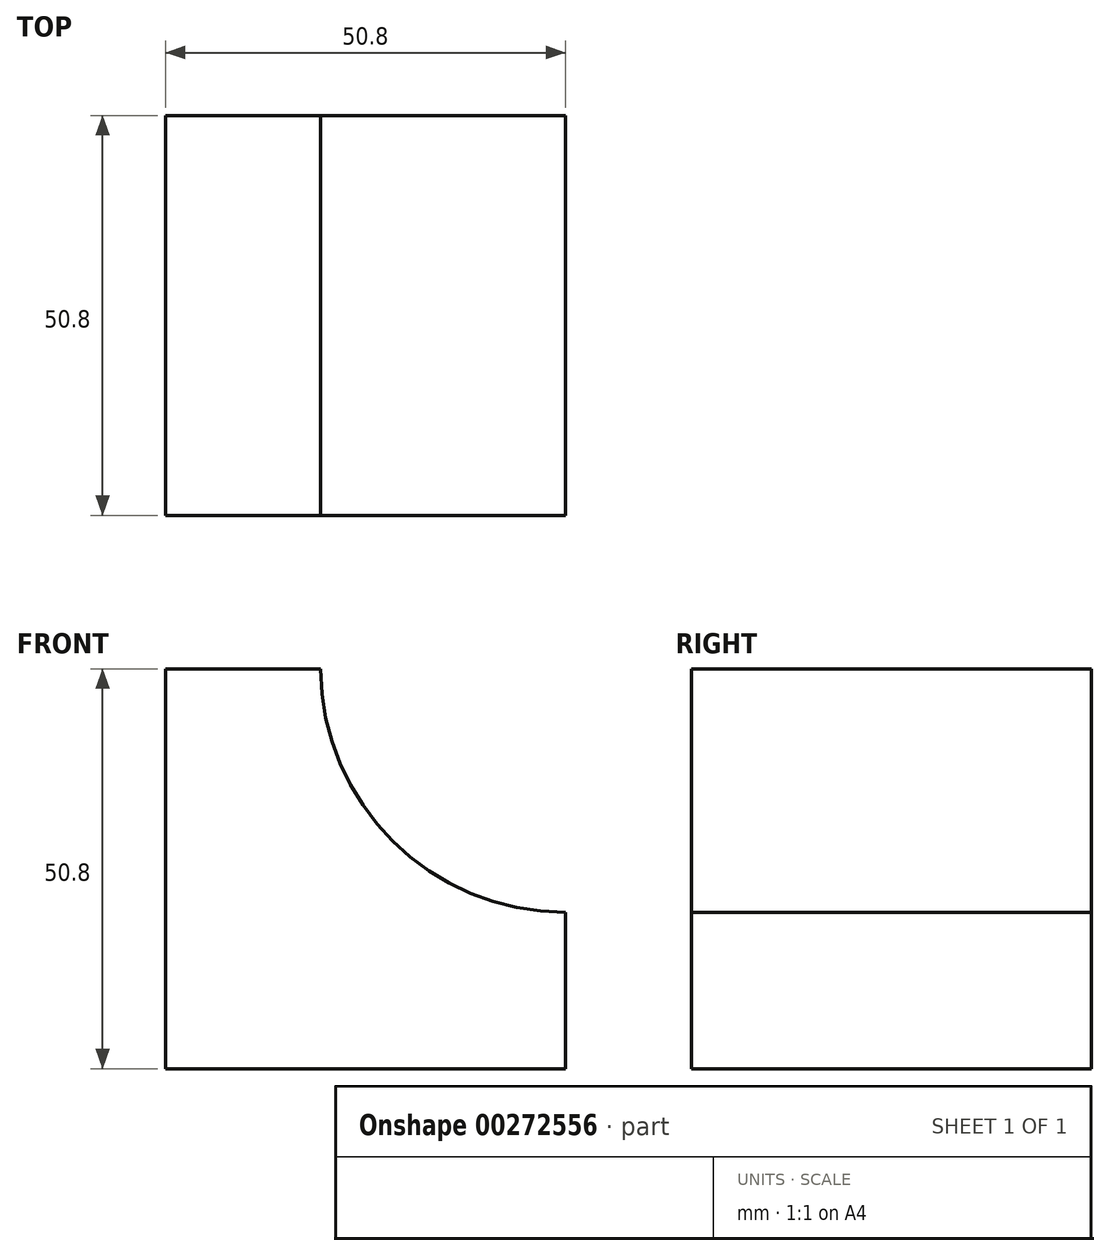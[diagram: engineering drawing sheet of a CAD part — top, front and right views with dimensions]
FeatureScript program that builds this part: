
annotation { "Feature Type Name" : "Feature", "Feature Type Description" : "" }
export const myFeature = defineFeature(function(context is Context, id is Id, definition is map)
    precondition{}
    {
        {
            var Q0;
            Q0=qCreatedBy(makeId("Front.planeOp"),FACE);
            var sketch = newSketch(context, id + "F0", { "sketchPlane" : qUnion([Q0])});
            skLineSegment(sketch, "E0", {"start": v(0, 0) * mm, "end": v(-50.8, 0) * mm});
            skLineSegment(sketch, "E1", {"start": v(-50.8, 0) * mm, "end": v(-50.8, 50.8) * mm});
            skLineSegment(sketch, "E2", {"start": v(-50.8, 50.8) * mm, "end": v(-31.13, 50.8) * mm});
            skLineSegment(sketch, "E3", {"start": v(0, 19.86) * mm, "end": v(0, 0) * mm});
            skArc(sketch, "E4", {"start": v(-31.13, 50.8) * mm, "mid": v(-21.94, 28.91) * mm, "end": v(0, 19.86) * mm});
            skSolve(sketch);
        }
        {
            var Q0;
            Q0=makeQuery(id+"F0.imprint","IMPRINT",FACE,{"disambiguationData":[TD([[makeQuery(id+"F0.imprint","IMPRINT",EDGE,{"derivedFrom":sQuery(id+"F0.wireOp",EDGE,"E0")}),-1.0]])]});
            extrude(context, id + "F1", {"entities" : qUnion([Q0]), "depth" : 50.8 * mm});
        }
    });
